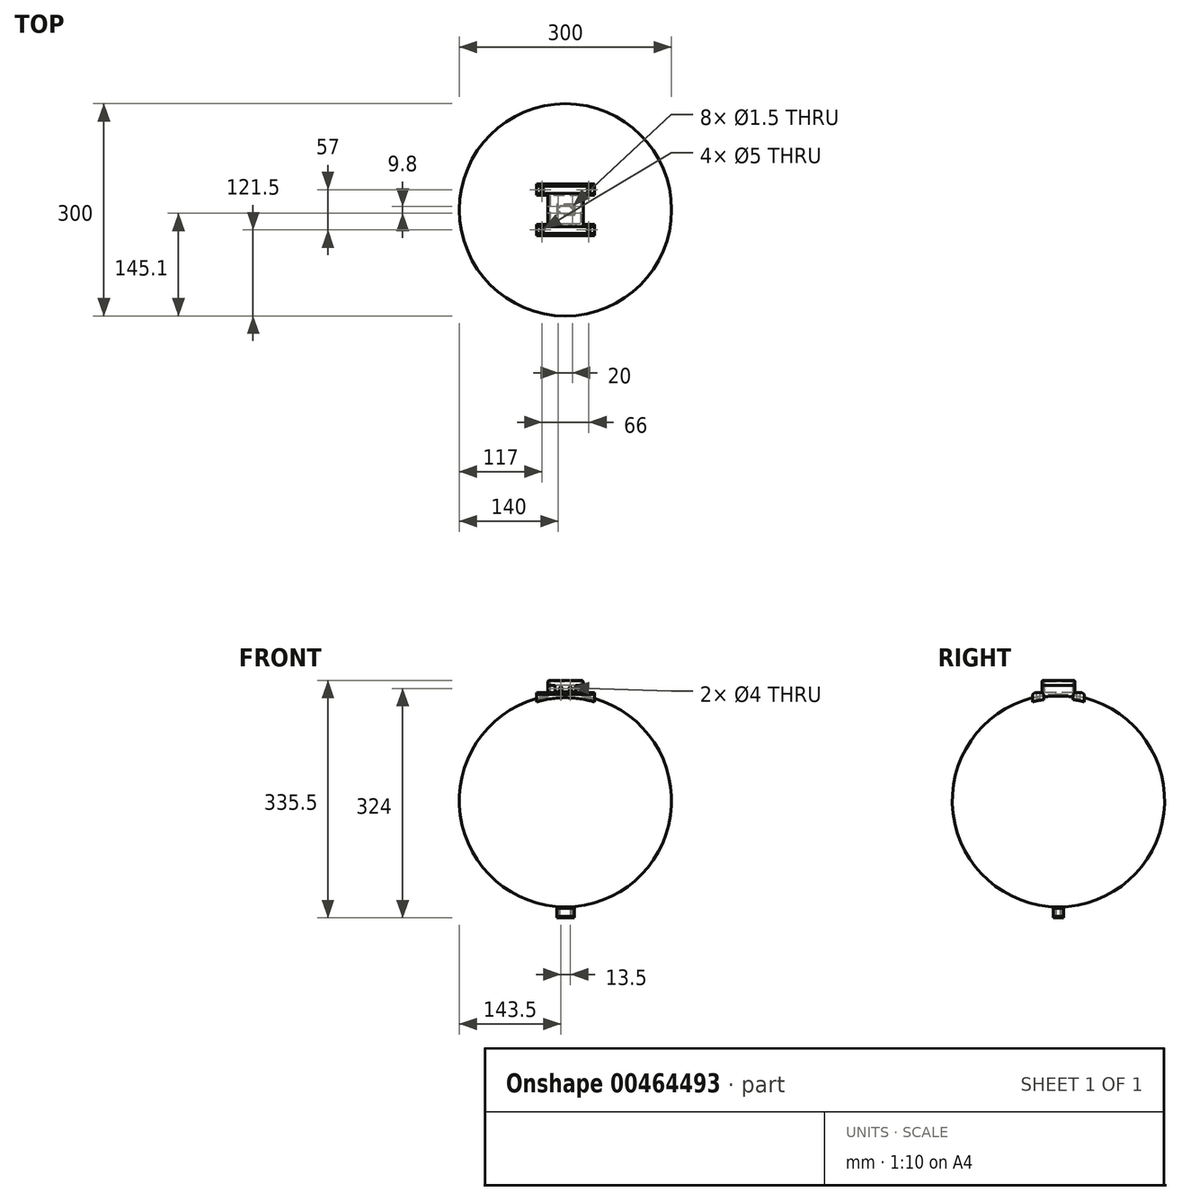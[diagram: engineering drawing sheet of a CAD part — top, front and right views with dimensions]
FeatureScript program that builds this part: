
annotation { "Feature Type Name" : "Feature", "Feature Type Description" : "" }
export const myFeature = defineFeature(function(context is Context, id is Id, definition is map)
    precondition{}
    {
        {
            assignVariable(context, id + "F0", {"name" : "R", "anyValue" : 150});
        }
        {
            assignVariable(context, id + "F1", {"name" : "T", "anyValue" : 3});
        }
        {
            assignVariable(context, id + "F2", {"name" : "t", "anyValue" : 2});
        }
        {
            var Q0;
            Q0=qCreatedBy(makeId("Right.planeOp"),FACE);
            var sketch = newSketch(context, id + "F3", { "sketchPlane" : qUnion([Q0])});
            skArc(sketch, "E0", {"start": v(0, -150) * mm, "mid": v(150, 0) * mm, "end": v(0, 150) * mm});
            skLineSegment(sketch, "E1", {"start": v(0, 133.29) * mm, "end": v(0, -166.2) * mm, "construction": true});
            skLineSegment(sketch, "E2", {"start": v(0, 150) * mm, "end": v(0, -150) * mm});
            skSolve(sketch);
        }
        {
            var Q0;
            Q0=makeQuery(id+"F3.imprint","IMPRINT",FACE,{"disambiguationData":[TD([[makeQuery(id+"F3.imprint","IMPRINT",EDGE,{"derivedFrom":sQuery(id+"F3.wireOp",EDGE,"E0")}),1.0]])]});
            var Q1;
            Q1=sQuery(id+"F3.wireOp",EDGE,"E1");
            revolve(context, id + "F4", {"entities" : qUnion([Q0]), "axis" : qUnion([Q1]), "revolveType" : RevolveType.FULL});
        }
        {
            var Q0;
            Q0=qCreatedBy(makeId("Top.planeOp"),FACE);
            cPlane(context, id + "F5", {"entities" : qUnion([Q0]), "cplaneType" : CPlaneType.OFFSET, "offset" : (getVariable(context, 'R') + getVariable(context, 'T')) * mm, "width" : 150 * mm, "height" : 150 * mm});
        }
        {
            var Q0;
            Q0=qCreatedBy(id+"F5.planeOp",FACE);
            var sketch = newSketch(context, id + "F6", { "sketchPlane" : qUnion([Q0])});
            skLineSegment(sketch, "E3.bottom", {"start": v(25, 36.5) * mm, "end": v(-25, 36.5) * mm});
            skLineSegment(sketch, "E3.top", {"start": v(25, -36.5) * mm, "end": v(-25, -36.5) * mm});
            skLineSegment(sketch, "E3.left", {"start": v(25, 20.5) * mm, "end": v(25, -20.5) * mm});
            skLineSegment(sketch, "E3.right", {"start": v(-25, 20.5) * mm, "end": v(-25, -20.5) * mm});
            skPoint(sketch, "E3.middle", {"position": v(0, 0) * mm});
            skLineSegment(sketch, "E4.bottom", {"start": v(-25, 36.5) * mm, "end": v(-41, 36.5) * mm});
            skLineSegment(sketch, "E4.top", {"start": v(-25, 20.5) * mm, "end": v(-41, 20.5) * mm});
            skLineSegment(sketch, "E4.right", {"start": v(-41, 36.5) * mm, "end": v(-41, 20.5) * mm});
            skLineSegment(sketch, "E5", {"start": v(0, 40.93) * mm, "end": v(0, -41.3) * mm, "construction": true});
            skLineSegment(sketch, "E6", {"start": v(40.69, 0) * mm, "end": v(-40.56, 0) * mm, "construction": true});
            skLineSegment(sketch, "E7.MirrorCS", {"start": v(25, 20.5) * mm, "end": v(41, 20.5) * mm});
            skLineSegment(sketch, "E8.MirrorCS", {"start": v(41, 36.5) * mm, "end": v(41, 20.5) * mm});
            skLineSegment(sketch, "E9.MirrorCS", {"start": v(25, 36.5) * mm, "end": v(41, 36.5) * mm});
            skLineSegment(sketch, "E10.MirrorCS", {"start": v(-25, -20.5) * mm, "end": v(-41, -20.5) * mm});
            skLineSegment(sketch, "E11.MirrorCS", {"start": v(-41, -36.5) * mm, "end": v(-41, -20.5) * mm});
            skLineSegment(sketch, "E12.MirrorCS", {"start": v(-25, -36.5) * mm, "end": v(-41, -36.5) * mm});
            skLineSegment(sketch, "E13.MirrorCS", {"start": v(25, -36.5) * mm, "end": v(41, -36.5) * mm});
            skLineSegment(sketch, "E14.MirrorCS", {"start": v(41, -36.5) * mm, "end": v(41, -20.5) * mm});
            skLineSegment(sketch, "E15.MirrorCS", {"start": v(25, -20.5) * mm, "end": v(41, -20.5) * mm});
            skLineSegment(sketch, "E16", {"start": v(-25, 20.5) * mm, "end": v(-41, 36.5) * mm, "construction": true});
            skLineSegment(sketch, "E17", {"start": v(-25, 36.5) * mm, "end": v(-41, 20.5) * mm, "construction": true});
            skCircle(sketch, "E18", {"center": v(-33, 28.5) * mm, "radius": 2.5 * mm});
            skCircle(sketch, "E19.MirrorC", {"center": v(33, 28.5) * mm, "radius": 2.5 * mm});
            skCircle(sketch, "E20.MirrorC", {"center": v(-33, -28.5) * mm, "radius": 2.5 * mm});
            skCircle(sketch, "E21.MirrorC", {"center": v(33, -28.5) * mm, "radius": 2.5 * mm});
            skSolve(sketch);
        }
        {
            var Q0;
            Q0=qSketchRegion(id+"F6",true);
            var Q1;
            Q1=makeQuery(id+"F4.opRevolve","SWEPT_FACE",FACE,{"disambiguationData":[OSD([sQuery(id+"F3.wireOp",EDGE,"E0")])]});
            extrude(context, id + "F7", {"entities" : qUnion([Q0]), "endBound" : BoundingType.UP_TO_SURFACE, "oppositeDirection" : true, "depth" : 25 * mm, "endBoundEntityFace" : qUnion([Q1]), "offsetDistance" : 25 * mm});
        }
        {
            var Q0;
            Q0=makeQuery(id+"F7.opExtrude","CAP_EDGE",EDGE,{"disambiguationData":[OSD([sQuery(id+"F6.wireOp",EDGE,"E3.bottom"),sQuery(id+"F6.wireOp",EDGE,"E4.bottom"),sQuery(id+"F6.wireOp",EDGE,"E9.MirrorCS")])],"isStart":true});
            var Q1;
            Q1=makeQuery(id+"F7.opExtrude","CAP_EDGE",EDGE,{"disambiguationData":[OSD([sQuery(id+"F6.wireOp",EDGE,"E3.top"),sQuery(id+"F6.wireOp",EDGE,"E12.MirrorCS"),sQuery(id+"F6.wireOp",EDGE,"E13.MirrorCS")])],"isStart":true});
            var Q2;
            Q2=makeQuery(id+"F7.opExtrude","CAP_EDGE",EDGE,{"disambiguationData":[OSD([sQuery(id+"F6.wireOp",EDGE,"E4.top")])],"isStart":true});
            var Q3;
            Q3=makeQuery(id+"F7.opExtrude","CAP_EDGE",EDGE,{"disambiguationData":[OSD([sQuery(id+"F6.wireOp",EDGE,"E7.MirrorCS")])],"isStart":true});
            var Q4;
            Q4=makeQuery(id+"F7.opExtrude","CAP_EDGE",EDGE,{"disambiguationData":[OSD([sQuery(id+"F6.wireOp",EDGE,"E15.MirrorCS")])],"isStart":true});
            var Q5;
            Q5=makeQuery(id+"F7.opExtrude","CAP_EDGE",EDGE,{"disambiguationData":[OSD([sQuery(id+"F6.wireOp",EDGE,"E10.MirrorCS")])],"isStart":true});
            chamfer(context, id + "F8", {"entities" : qUnion([Q0, Q1, Q2, Q3, Q4, Q5]), "width" : 3 * mm, "tangentPropagation" : true});
        }
        {
            var Q0;
            Q0=makeQuery(id+"F7.opExtrude","CAP_FACE",FACE,{"disambiguationData":[OSD([sQuery(id+"F6.wireOp",EDGE,"E3.bottom"),sQuery(id+"F6.wireOp",EDGE,"E3.top"),sQuery(id+"F6.wireOp",EDGE,"E3.left"),sQuery(id+"F6.wireOp",EDGE,"E3.right"),sQuery(id+"F6.wireOp",EDGE,"E4.bottom"),sQuery(id+"F6.wireOp",EDGE,"E4.top"),sQuery(id+"F6.wireOp",EDGE,"E4.right"),sQuery(id+"F6.wireOp",EDGE,"E7.MirrorCS"),sQuery(id+"F6.wireOp",EDGE,"E8.MirrorCS"),sQuery(id+"F6.wireOp",EDGE,"E9.MirrorCS"),sQuery(id+"F6.wireOp",EDGE,"E10.MirrorCS"),sQuery(id+"F6.wireOp",EDGE,"E11.MirrorCS"),sQuery(id+"F6.wireOp",EDGE,"E12.MirrorCS"),sQuery(id+"F6.wireOp",EDGE,"E13.MirrorCS"),sQuery(id+"F6.wireOp",EDGE,"E14.MirrorCS"),sQuery(id+"F6.wireOp",EDGE,"E15.MirrorCS"),sQuery(id+"F6.wireOp",EDGE,"E18"),sQuery(id+"F6.wireOp",EDGE,"E19.MirrorC"),sQuery(id+"F6.wireOp",EDGE,"E20.MirrorC"),sQuery(id+"F6.wireOp",EDGE,"E21.MirrorC")])],"isStart":true});
            var sketch = newSketch(context, id + "F9", { "sketchPlane" : qUnion([Q0])});
            skLineSegment(sketch, "E22.bottom", {"start": v(25, 23.5) * mm, "end": v(-25, 23.5) * mm});
            skLineSegment(sketch, "E22.top", {"start": v(25, -23.5) * mm, "end": v(15, -23.5) * mm});
            skLineSegment(sketch, "E22.left", {"start": v(25, 23.5) * mm, "end": v(25, -23.5) * mm});
            skLineSegment(sketch, "E22.right", {"start": v(-25, 23.5) * mm, "end": v(-25, -23.5) * mm});
            skPoint(sketch, "E22.middle", {"position": v(0, 0) * mm});
            skLineSegment(sketch, "E23.0", {"start": v(21.5, 20) * mm, "end": v(-21.5, 20) * mm});
            skLineSegment(sketch, "E23.1", {"start": v(21.5, 20) * mm, "end": v(21.5, -20) * mm});
            skLineSegment(sketch, "E23.2", {"start": v(21.5, -20) * mm, "end": v(15, -20) * mm});
            skLineSegment(sketch, "E23.3", {"start": v(-21.5, 20) * mm, "end": v(-21.5, -20) * mm});
            skLineSegment(sketch, "E24", {"start": v(-15, -20) * mm, "end": v(-15, -23.5) * mm});
            skLineSegment(sketch, "E25", {"start": v(15, -20) * mm, "end": v(15, -23.5) * mm});
            skLineSegment(sketch, "E26.trimOffspring", {"start": v(-15, -20) * mm, "end": v(-21.5, -20) * mm});
            skLineSegment(sketch, "E27.trimOffspring", {"start": v(-15, -23.5) * mm, "end": v(-25, -23.5) * mm});
            skSolve(sketch);
        }
        {
            var Q0;
            Q0=qSketchRegion(id+"F9",true);
            extrude(context, id + "F10", {"entities" : qUnion([Q0]), "operationType" : NewBodyOperationType.ADD, "depth" : 10 * mm, "offsetDistance" : 25 * mm});
        }
        {
            var Q0;
            Q0=makeQuery(id+"F10.opExtrude","CAP_FACE",FACE,{"disambiguationData":[OSD([sQuery(id+"F9.wireOp",EDGE,"E22.bottom"),sQuery(id+"F9.wireOp",EDGE,"E22.top"),sQuery(id+"F9.wireOp",EDGE,"E22.left"),sQuery(id+"F9.wireOp",EDGE,"E22.right"),sQuery(id+"F9.wireOp",EDGE,"E23.0"),sQuery(id+"F9.wireOp",EDGE,"E23.1"),sQuery(id+"F9.wireOp",EDGE,"E23.2"),sQuery(id+"F9.wireOp",EDGE,"E23.3"),sQuery(id+"F9.wireOp",EDGE,"E24"),sQuery(id+"F9.wireOp",EDGE,"E25"),sQuery(id+"F9.wireOp",EDGE,"E26.trimOffspring"),sQuery(id+"F9.wireOp",EDGE,"E27.trimOffspring")])],"isStart":false});
            var sketch = newSketch(context, id + "F11", { "sketchPlane" : qUnion([Q0])});
            skLineSegment(sketch, "E28.bottom", {"start": v(25, 23.5) * mm, "end": v(-25, 23.5) * mm});
            skLineSegment(sketch, "E28.top", {"start": v(25, -23.5) * mm, "end": v(-25, -23.5) * mm});
            skLineSegment(sketch, "E28.left", {"start": v(25, 23.5) * mm, "end": v(25, -23.5) * mm});
            skLineSegment(sketch, "E28.right", {"start": v(-25, 23.5) * mm, "end": v(-25, -23.5) * mm});
            skPoint(sketch, "E28.middle", {"position": v(0, 0) * mm});
            skLineSegment(sketch, "E29.0", {"start": v(21.5, 20) * mm, "end": v(-21.5, 20) * mm});
            skLineSegment(sketch, "E29.1", {"start": v(21.5, 20) * mm, "end": v(21.5, -20) * mm});
            skLineSegment(sketch, "E29.2", {"start": v(21.5, -20) * mm, "end": v(-21.5, -20) * mm});
            skLineSegment(sketch, "E29.3", {"start": v(-21.5, 20) * mm, "end": v(-21.5, -20) * mm});
            skSolve(sketch);
        }
        {
            var Q0;
            Q0=qSketchRegion(id+"F11",true);
            extrude(context, id + "F12", {"entities" : qUnion([Q0]), "depth" : 5 * mm, "offsetDistance" : 25 * mm});
        }
        {
            var Q0;
            Q0=makeQuery(id+"F12.opExtrude","CAP_FACE",FACE,{"disambiguationData":[OSD([sQuery(id+"F11.wireOp",EDGE,"E28.bottom"),sQuery(id+"F11.wireOp",EDGE,"E28.top"),sQuery(id+"F11.wireOp",EDGE,"E28.left"),sQuery(id+"F11.wireOp",EDGE,"E28.right"),sQuery(id+"F11.wireOp",EDGE,"E29.0"),sQuery(id+"F11.wireOp",EDGE,"E29.1"),sQuery(id+"F11.wireOp",EDGE,"E29.2"),sQuery(id+"F11.wireOp",EDGE,"E29.3")])],"isStart":false});
            var sketch = newSketch(context, id + "F13", { "sketchPlane" : qUnion([Q0])});
            skLineSegment(sketch, "E30.bottom", {"start": v(25, 23.5) * mm, "end": v(-25, 23.5) * mm});
            skLineSegment(sketch, "E30.top", {"start": v(25, -23.5) * mm, "end": v(-25, -23.5) * mm});
            skLineSegment(sketch, "E30.left", {"start": v(25, 23.5) * mm, "end": v(25, -23.5) * mm});
            skLineSegment(sketch, "E30.right", {"start": v(-25, 23.5) * mm, "end": v(-25, -23.5) * mm});
            skPoint(sketch, "E30.middle", {"position": v(0, 0) * mm});
            skSolve(sketch);
        }
        {
            var Q0;
            Q0=qSketchRegion(id+"F13",true);
            extrude(context, id + "F14", {"entities" : qUnion([Q0]), "operationType" : NewBodyOperationType.ADD, "depth" : 2 * mm, "offsetDistance" : 25 * mm});
        }
        {
            var Q0;
            Q0=makeQuery(id+"F14.opExtrude","CAP_FACE",FACE,{"disambiguationData":[OSD([sQuery(id+"F13.wireOp",EDGE,"E30.bottom"),sQuery(id+"F13.wireOp",EDGE,"E30.top"),sQuery(id+"F13.wireOp",EDGE,"E30.left"),sQuery(id+"F13.wireOp",EDGE,"E30.right")])],"isStart":false});
            var Q1;
            Q1=makeQuery(id+"F14.boolean.opBoolean","MERGE",EDGE,{"derivedFrom":[makeQuery(id+"F12.opExtrude","SWEPT_EDGE",EDGE,{"disambiguationData":[OSD([sQuery(id+"F11.wireOp",EDGE,"E28.top"),sQuery(id+"F11.wireOp",EDGE,"E28.right")])]}),makeQuery(id+"F14.opExtrude","SWEPT_EDGE",EDGE,{"disambiguationData":[OSD([sQuery(id+"F13.wireOp",EDGE,"E30.top"),sQuery(id+"F13.wireOp",EDGE,"E30.right")])]})]});
            var Q2;
            Q2=makeQuery(id+"F10.opExtrude","SWEPT_EDGE",EDGE,{"disambiguationData":[OSD([sQuery(id+"F6.wireOp",EDGE,"E3.bottom"),sQuery(id+"F6.wireOp",EDGE,"E3.top"),sQuery(id+"F6.wireOp",EDGE,"E3.left"),sQuery(id+"F6.wireOp",EDGE,"E3.right"),sQuery(id+"F6.wireOp",EDGE,"E4.bottom"),sQuery(id+"F6.wireOp",EDGE,"E4.top"),sQuery(id+"F6.wireOp",EDGE,"E4.right"),sQuery(id+"F6.wireOp",EDGE,"E7.MirrorCS"),sQuery(id+"F6.wireOp",EDGE,"E8.MirrorCS"),sQuery(id+"F6.wireOp",EDGE,"E9.MirrorCS"),sQuery(id+"F6.wireOp",EDGE,"E10.MirrorCS"),sQuery(id+"F6.wireOp",EDGE,"E11.MirrorCS"),sQuery(id+"F6.wireOp",EDGE,"E12.MirrorCS"),sQuery(id+"F6.wireOp",EDGE,"E13.MirrorCS"),sQuery(id+"F6.wireOp",EDGE,"E14.MirrorCS"),sQuery(id+"F6.wireOp",EDGE,"E15.MirrorCS"),sQuery(id+"F6.wireOp",EDGE,"E18"),sQuery(id+"F6.wireOp",EDGE,"E19.MirrorC"),sQuery(id+"F6.wireOp",EDGE,"E20.MirrorC"),sQuery(id+"F6.wireOp",EDGE,"E21.MirrorC"),sQuery(id+"F9.wireOp",EDGE,"E22.right"),sQuery(id+"F9.wireOp",EDGE,"E27.trimOffspring")])]});
            var Q3;
            Q3=makeQuery(id+"F10.opExtrude","SWEPT_EDGE",EDGE,{"disambiguationData":[OSD([sQuery(id+"F6.wireOp",EDGE,"E3.bottom"),sQuery(id+"F6.wireOp",EDGE,"E3.top"),sQuery(id+"F6.wireOp",EDGE,"E3.left"),sQuery(id+"F6.wireOp",EDGE,"E3.right"),sQuery(id+"F6.wireOp",EDGE,"E4.bottom"),sQuery(id+"F6.wireOp",EDGE,"E4.top"),sQuery(id+"F6.wireOp",EDGE,"E4.right"),sQuery(id+"F6.wireOp",EDGE,"E7.MirrorCS"),sQuery(id+"F6.wireOp",EDGE,"E8.MirrorCS"),sQuery(id+"F6.wireOp",EDGE,"E9.MirrorCS"),sQuery(id+"F6.wireOp",EDGE,"E10.MirrorCS"),sQuery(id+"F6.wireOp",EDGE,"E11.MirrorCS"),sQuery(id+"F6.wireOp",EDGE,"E12.MirrorCS"),sQuery(id+"F6.wireOp",EDGE,"E13.MirrorCS"),sQuery(id+"F6.wireOp",EDGE,"E14.MirrorCS"),sQuery(id+"F6.wireOp",EDGE,"E15.MirrorCS"),sQuery(id+"F6.wireOp",EDGE,"E18"),sQuery(id+"F6.wireOp",EDGE,"E19.MirrorC"),sQuery(id+"F6.wireOp",EDGE,"E20.MirrorC"),sQuery(id+"F6.wireOp",EDGE,"E21.MirrorC"),sQuery(id+"F9.wireOp",EDGE,"E22.bottom"),sQuery(id+"F9.wireOp",EDGE,"E22.right")])]});
            var Q4;
            Q4=makeQuery(id+"F14.boolean.opBoolean","MERGE",EDGE,{"derivedFrom":[makeQuery(id+"F12.opExtrude","SWEPT_EDGE",EDGE,{"disambiguationData":[OSD([sQuery(id+"F11.wireOp",EDGE,"E28.bottom"),sQuery(id+"F11.wireOp",EDGE,"E28.right")])]}),makeQuery(id+"F14.opExtrude","SWEPT_EDGE",EDGE,{"disambiguationData":[OSD([sQuery(id+"F13.wireOp",EDGE,"E30.bottom"),sQuery(id+"F13.wireOp",EDGE,"E30.right")])]})]});
            var Q5;
            Q5=makeQuery(id+"F10.opExtrude","SWEPT_EDGE",EDGE,{"disambiguationData":[OSD([sQuery(id+"F6.wireOp",EDGE,"E3.bottom"),sQuery(id+"F6.wireOp",EDGE,"E3.top"),sQuery(id+"F6.wireOp",EDGE,"E3.left"),sQuery(id+"F6.wireOp",EDGE,"E3.right"),sQuery(id+"F6.wireOp",EDGE,"E4.bottom"),sQuery(id+"F6.wireOp",EDGE,"E4.top"),sQuery(id+"F6.wireOp",EDGE,"E4.right"),sQuery(id+"F6.wireOp",EDGE,"E7.MirrorCS"),sQuery(id+"F6.wireOp",EDGE,"E8.MirrorCS"),sQuery(id+"F6.wireOp",EDGE,"E9.MirrorCS"),sQuery(id+"F6.wireOp",EDGE,"E10.MirrorCS"),sQuery(id+"F6.wireOp",EDGE,"E11.MirrorCS"),sQuery(id+"F6.wireOp",EDGE,"E12.MirrorCS"),sQuery(id+"F6.wireOp",EDGE,"E13.MirrorCS"),sQuery(id+"F6.wireOp",EDGE,"E14.MirrorCS"),sQuery(id+"F6.wireOp",EDGE,"E15.MirrorCS"),sQuery(id+"F6.wireOp",EDGE,"E18"),sQuery(id+"F6.wireOp",EDGE,"E19.MirrorC"),sQuery(id+"F6.wireOp",EDGE,"E20.MirrorC"),sQuery(id+"F6.wireOp",EDGE,"E21.MirrorC"),sQuery(id+"F9.wireOp",EDGE,"E22.top"),sQuery(id+"F9.wireOp",EDGE,"E22.left")])]});
            var Q6;
            Q6=makeQuery(id+"F14.boolean.opBoolean","MERGE",EDGE,{"derivedFrom":[makeQuery(id+"F12.opExtrude","SWEPT_EDGE",EDGE,{"disambiguationData":[OSD([sQuery(id+"F11.wireOp",EDGE,"E28.top"),sQuery(id+"F11.wireOp",EDGE,"E28.left")])]}),makeQuery(id+"F14.opExtrude","SWEPT_EDGE",EDGE,{"disambiguationData":[OSD([sQuery(id+"F13.wireOp",EDGE,"E30.top"),sQuery(id+"F13.wireOp",EDGE,"E30.left")])]})]});
            var Q7;
            Q7=makeQuery(id+"F10.opExtrude","SWEPT_EDGE",EDGE,{"disambiguationData":[OSD([sQuery(id+"F6.wireOp",EDGE,"E3.bottom"),sQuery(id+"F6.wireOp",EDGE,"E3.top"),sQuery(id+"F6.wireOp",EDGE,"E3.left"),sQuery(id+"F6.wireOp",EDGE,"E3.right"),sQuery(id+"F6.wireOp",EDGE,"E4.bottom"),sQuery(id+"F6.wireOp",EDGE,"E4.top"),sQuery(id+"F6.wireOp",EDGE,"E4.right"),sQuery(id+"F6.wireOp",EDGE,"E7.MirrorCS"),sQuery(id+"F6.wireOp",EDGE,"E8.MirrorCS"),sQuery(id+"F6.wireOp",EDGE,"E9.MirrorCS"),sQuery(id+"F6.wireOp",EDGE,"E10.MirrorCS"),sQuery(id+"F6.wireOp",EDGE,"E11.MirrorCS"),sQuery(id+"F6.wireOp",EDGE,"E12.MirrorCS"),sQuery(id+"F6.wireOp",EDGE,"E13.MirrorCS"),sQuery(id+"F6.wireOp",EDGE,"E14.MirrorCS"),sQuery(id+"F6.wireOp",EDGE,"E15.MirrorCS"),sQuery(id+"F6.wireOp",EDGE,"E18"),sQuery(id+"F6.wireOp",EDGE,"E19.MirrorC"),sQuery(id+"F6.wireOp",EDGE,"E20.MirrorC"),sQuery(id+"F6.wireOp",EDGE,"E21.MirrorC"),sQuery(id+"F9.wireOp",EDGE,"E22.bottom"),sQuery(id+"F9.wireOp",EDGE,"E22.left")])]});
            var Q8;
            Q8=makeQuery(id+"F14.boolean.opBoolean","MERGE",EDGE,{"derivedFrom":[makeQuery(id+"F12.opExtrude","SWEPT_EDGE",EDGE,{"disambiguationData":[OSD([sQuery(id+"F11.wireOp",EDGE,"E28.bottom"),sQuery(id+"F11.wireOp",EDGE,"E28.left")])]}),makeQuery(id+"F14.opExtrude","SWEPT_EDGE",EDGE,{"disambiguationData":[OSD([sQuery(id+"F13.wireOp",EDGE,"E30.bottom"),sQuery(id+"F13.wireOp",EDGE,"E30.left")])]})]});
            fillet(context, id + "F15", {"entities" : qUnion([Q0, Q1, Q2, Q3, Q4, Q5, Q6, Q7, Q8]), "radius" : 2.5 * mm, "tangentPropagation" : true, "allowEdgeOverflow" : false});
        }
        {
            var Q0;
            Q0=makeQuery(id+"F12.opExtrude","CAP_FACE",FACE,{"disambiguationData":[OSD([sQuery(id+"F11.wireOp",EDGE,"E28.bottom"),sQuery(id+"F11.wireOp",EDGE,"E28.top"),sQuery(id+"F11.wireOp",EDGE,"E28.left"),sQuery(id+"F11.wireOp",EDGE,"E28.right"),sQuery(id+"F11.wireOp",EDGE,"E29.0"),sQuery(id+"F11.wireOp",EDGE,"E29.1"),sQuery(id+"F11.wireOp",EDGE,"E29.2"),sQuery(id+"F11.wireOp",EDGE,"E29.3")])],"isStart":true});
            var sketch = newSketch(context, id + "F16", { "sketchPlane" : qUnion([Q0])});
            skLineSegment(sketch, "E31.bottom", {"start": v(-14.5, 23.5) * mm, "end": v(14.5, 23.5) * mm});
            skLineSegment(sketch, "E31.top", {"start": v(-14.5, 20) * mm, "end": v(14.5, 20) * mm});
            skLineSegment(sketch, "E31.left", {"start": v(-14.5, 23.5) * mm, "end": v(-14.5, 20) * mm});
            skLineSegment(sketch, "E31.right", {"start": v(14.5, 23.5) * mm, "end": v(14.5, 20) * mm});
            skSolve(sketch);
        }
        {
            var Q0;
            Q0=qSketchRegion(id+"F16",true);
            extrude(context, id + "F17", {"entities" : qUnion([Q0]), "operationType" : NewBodyOperationType.ADD, "depth" : 9 * mm, "offsetDistance" : 25 * mm});
        }
        {
            var Q0;
            Q0=makeQuery(id+"F17.boolean.opBoolean","MERGE",FACE,{"derivedFrom":[makeQuery(id+"F14.boolean.opBoolean","MERGE",FACE,{"derivedFrom":[makeQuery(id+"F12.opExtrude","SWEPT_FACE",FACE,{"disambiguationData":[OSD([sQuery(id+"F11.wireOp",EDGE,"E28.top")])]}),makeQuery(id+"F14.opExtrude","SWEPT_FACE",FACE,{"disambiguationData":[OSD([sQuery(id+"F13.wireOp",EDGE,"E30.top")])]})]}),makeQuery(id+"F17.opExtrude","SWEPT_FACE",FACE,{"disambiguationData":[OSD([sQuery(id+"F16.wireOp",EDGE,"E31.bottom")])]})]});
            var sketch = newSketch(context, id + "F18", { "sketchPlane" : qUnion([Q0])});
            skCircle(sketch, "E32", {"center": v(-6.5, 158.5) * mm, "radius": 2 * mm});
            skCircle(sketch, "E33", {"center": v(7, 158.5) * mm, "radius": 2 * mm});
            skSolve(sketch);
        }
        {
            var Q0;
            Q0=qSketchRegion(id+"F18",true);
            var Q1;
            Q1=makeQuery(id+"F17.boolean.opBoolean","MERGE",FACE,{"derivedFrom":[makeQuery(id+"F12.opExtrude","SWEPT_FACE",FACE,{"disambiguationData":[OSD([sQuery(id+"F11.wireOp",EDGE,"E29.2")])]}),makeQuery(id+"F17.opExtrude","SWEPT_FACE",FACE,{"disambiguationData":[OSD([sQuery(id+"F16.wireOp",EDGE,"E31.top")])]})]});
            extrude(context, id + "F19", {"entities" : qUnion([Q0]), "operationType" : NewBodyOperationType.REMOVE, "endBound" : BoundingType.UP_TO_SURFACE, "oppositeDirection" : true, "depth" : 25 * mm, "endBoundEntityFace" : qUnion([Q1]), "offsetDistance" : 25 * mm});
        }
        {
            var Q0;
            Q0=qCreatedBy(makeId("Top.planeOp"),FACE);
            cPlane(context, id + "F20", {"entities" : qUnion([Q0]), "cplaneType" : CPlaneType.OFFSET, "offset" : (getVariable(context, 'R') + getVariable(context, 't')) * mm, "oppositeDirection" : true, "width" : 150 * mm, "height" : 150 * mm});
        }
        {
            var Q0;
            Q0=qCreatedBy(id+"F20.planeOp",FACE);
            var sketch = newSketch(context, id + "F21", { "sketchPlane" : qUnion([Q0])});
            skLineSegment(sketch, "E34.bottom", {"start": v(12.5, 7.15) * mm, "end": v(-12.5, 7.15) * mm});
            skLineSegment(sketch, "E34.top", {"start": v(12.5, -7.15) * mm, "end": v(-12.5, -7.15) * mm});
            skLineSegment(sketch, "E34.left", {"start": v(12.5, 7.15) * mm, "end": v(12.5, -7.15) * mm});
            skLineSegment(sketch, "E34.right", {"start": v(-12.5, 7.15) * mm, "end": v(-12.5, -7.15) * mm});
            skPoint(sketch, "E34.middle", {"position": v(0, 0) * mm});
            skLineSegment(sketch, "E35.0", {"start": v(13.5, -8.15) * mm, "end": v(-12.5, -8.15) * mm});
            skLineSegment(sketch, "E35.1", {"start": v(13.5, 8.15) * mm, "end": v(13.5, -8.15) * mm});
            skLineSegment(sketch, "E35.2", {"start": v(13.5, 8.15) * mm, "end": v(-12.5, 8.15) * mm});
            skLineSegment(sketch, "E36", {"start": v(-12.5, -8.15) * mm, "end": v(-12.5, -7.15) * mm});
            skLineSegment(sketch, "E37", {"start": v(-12.5, 8.15) * mm, "end": v(-12.5, 7.15) * mm});
            skSolve(sketch);
        }
        {
            var Q0;
            Q0=qSketchRegion(id+"F21",true);
            extrude(context, id + "F22", {"entities" : qUnion([Q0]), "depth" : 1 * mm, "offsetDistance" : 25 * mm});
        }
        {
            var Q0;
            Q0=makeQuery(id+"F21.imprint","IMPRINT",FACE,{"disambiguationData":[TD([[makeQuery(id+"F21.imprint","IMPRINT",EDGE,{"derivedFrom":sQuery(id+"F21.wireOp",EDGE,"E34.bottom")}),1.0]])]});
            extrude(context, id + "F23", {"entities" : qUnion([Q0]), "operationType" : NewBodyOperationType.ADD, "oppositeDirection" : true, "depth" : 1.5 * mm, "offsetDistance" : 25 * mm});
        }
        {
            var Q0;
            Q0=makeQuery(id+"F23.opExtrude","CAP_FACE",FACE,{"disambiguationData":[OSD([sQuery(id+"F21.wireOp",EDGE,"E34.bottom"),sQuery(id+"F21.wireOp",EDGE,"E34.top"),sQuery(id+"F21.wireOp",EDGE,"E34.left"),sQuery(id+"F21.wireOp",EDGE,"E34.right")])],"isStart":false});
            var sketch = newSketch(context, id + "F24", { "sketchPlane" : qUnion([Q0])});
            skLineSegment(sketch, "E38.bottom", {"start": v(12.5, 7.15) * mm, "end": v(-12.5, 7.15) * mm});
            skLineSegment(sketch, "E38.top", {"start": v(12.5, -7.15) * mm, "end": v(-12.5, -7.15) * mm});
            skLineSegment(sketch, "E38.left", {"start": v(12.5, 7.15) * mm, "end": v(12.5, -7.15) * mm});
            skLineSegment(sketch, "E38.right", {"start": v(-12.5, 7.15) * mm, "end": v(-12.5, 3) * mm});
            skPoint(sketch, "E38.middle", {"position": v(0, 0) * mm});
            skLineSegment(sketch, "E39.0", {"start": v(7.5, 5.65) * mm, "end": v(-7.5, 5.65) * mm});
            skLineSegment(sketch, "E39.1", {"start": v(11, 3) * mm, "end": v(11, -3) * mm});
            skLineSegment(sketch, "E39.2", {"start": v(7.5, -5.65) * mm, "end": v(-7.5, -5.65) * mm});
            skLineSegment(sketch, "E40", {"start": v(-7.5, 3) * mm, "end": v(-12.5, 3) * mm});
            skLineSegment(sketch, "E41.trimOffspring", {"start": v(-12.5, -3) * mm, "end": v(-12.5, -7.15) * mm});
            skLineSegment(sketch, "E42", {"start": v(-7.5, 3) * mm, "end": v(-7.5, 5.65) * mm});
            skLineSegment(sketch, "E43", {"start": v(-12.5, 0) * mm, "end": v(12.5, 0) * mm, "construction": true});
            skLineSegment(sketch, "E44", {"start": v(0, 7.15) * mm, "end": v(0, -7.15) * mm, "construction": true});
            skLineSegment(sketch, "E45.MirrorCS", {"start": v(7.5, 3) * mm, "end": v(7.5, 5.65) * mm});
            skLineSegment(sketch, "E46.MirrorCS", {"start": v(7.5, 3) * mm, "end": v(12.5, 3) * mm});
            skLineSegment(sketch, "E47.MirrorCS", {"start": v(7.5, -3) * mm, "end": v(7.5, -5.65) * mm});
            skLineSegment(sketch, "E48.MirrorCS", {"start": v(7.5, -3) * mm, "end": v(12.5, -3) * mm});
            skLineSegment(sketch, "E49.MirrorCS", {"start": v(-7.5, -3) * mm, "end": v(-7.5, -5.65) * mm});
            skLineSegment(sketch, "E50.MirrorCS", {"start": v(-7.5, -3) * mm, "end": v(-12.5, -3) * mm});
            skSolve(sketch);
        }
        {
            var Q0;
            Q0=qSketchRegion(id+"F24",true);
            extrude(context, id + "F25", {"entities" : qUnion([Q0]), "operationType" : NewBodyOperationType.ADD, "depth" : 10 * mm, "offsetDistance" : 25 * mm});
        }
        {
            var Q0;
            Q0=makeQuery(id+"F25.opExtrude","CAP_FACE",FACE,{"disambiguationData":[OSD([sQuery(id+"F24.wireOp",EDGE,"E38.bottom"),sQuery(id+"F24.wireOp",EDGE,"E38.top"),sQuery(id+"F24.wireOp",EDGE,"E38.left"),sQuery(id+"F24.wireOp",EDGE,"E38.right"),sQuery(id+"F24.wireOp",EDGE,"E39.0"),sQuery(id+"F24.wireOp",EDGE,"E39.1"),sQuery(id+"F24.wireOp",EDGE,"E39.2"),sQuery(id+"F24.wireOp",EDGE,"E39.3"),sQuery(id+"F24.wireOp",EDGE,"q1GNPKCj-zdpP-4HE7-qGwj-qCHKBDN4xecH.bottom"),sQuery(id+"F24.wireOp",EDGE,"q1GNPKCj-zdpP-4HE7-qGwj-qCHKBDN4xecH.top"),sQuery(id+"F24.wireOp",EDGE,"q1GNPKCj-zdpP-4HE7-qGwj-qCHKBDN4xecH.left"),sQuery(id+"F24.wireOp",EDGE,"q1GNPKCj-zdpP-4HE7-qGwj-qCHKBDN4xecH.right"),sQuery(id+"F24.wireOp",EDGE,"9ayAVEPv-Baah-zfO2-cBUv-Tw3wUvXcA2ry.bottom"),sQuery(id+"F24.wireOp",EDGE,"9ayAVEPv-Baah-zfO2-cBUv-Tw3wUvXcA2ry.top"),sQuery(id+"F24.wireOp",EDGE,"9ayAVEPv-Baah-zfO2-cBUv-Tw3wUvXcA2ry.right"),sQuery(id+"F24.wireOp",EDGE,"KkwPjkcE-YuFN-ka4I-ebTg-GOtfCpxhzfaz.bottom"),sQuery(id+"F24.wireOp",EDGE,"KkwPjkcE-YuFN-ka4I-ebTg-GOtfCpxhzfaz.top"),sQuery(id+"F24.wireOp",EDGE,"KkwPjkcE-YuFN-ka4I-ebTg-GOtfCpxhzfaz.left"),sQuery(id+"F24.wireOp",EDGE,"KkwPjkcE-YuFN-ka4I-ebTg-GOtfCpxhzfaz.right"),sQuery(id+"F24.wireOp",EDGE,"bSv0btmW-40Pc-zO7x-vEyI-oRbhWPC2zANg.bottom"),sQuery(id+"F24.wireOp",EDGE,"bSv0btmW-40Pc-zO7x-vEyI-oRbhWPC2zANg.top"),sQuery(id+"F24.wireOp",EDGE,"bSv0btmW-40Pc-zO7x-vEyI-oRbhWPC2zANg.left"),sQuery(id+"F24.wireOp",EDGE,"bSv0btmW-40Pc-zO7x-vEyI-oRbhWPC2zANg.right"),sQuery(id+"F24.wireOp",EDGE,"E40"),sQuery(id+"F24.wireOp",EDGE,"pJDALD0U-aj2j-U3tK-gEwn-GPk6D3x3Uf9U"),sQuery(id+"F24.wireOp",EDGE,"8bf2260b-e43b-4eec-a6cd-762596e679c8.trimOffspring"),sQuery(id+"F24.wireOp",EDGE,"E41.trimOffspring")])],"isStart":false});
            var sketch = newSketch(context, id + "F26", { "sketchPlane" : qUnion([Q0])});
            skLineSegment(sketch, "E51.bottom", {"start": v(-12.5, 7.15) * mm, "end": v(12.5, 7.15) * mm});
            skLineSegment(sketch, "E51.top", {"start": v(-12.5, -7.15) * mm, "end": v(12.5, -7.15) * mm});
            skLineSegment(sketch, "E51.left", {"start": v(-12.5, 7.15) * mm, "end": v(-12.5, -7.15) * mm});
            skLineSegment(sketch, "E51.right", {"start": v(12.5, 7.15) * mm, "end": v(12.5, -7.15) * mm});
            skSolve(sketch);
        }
        {
            var Q0;
            Q0=qSketchRegion(id+"F26",true);
            extrude(context, id + "F27", {"entities" : qUnion([Q0]), "depth" : 2 * mm, "offsetDistance" : 25 * mm});
        }
        {
            var Q0;
            Q0=makeQuery(id+"F27.opExtrude","CAP_FACE",FACE,{"disambiguationData":[OSD([sQuery(id+"F26.wireOp",EDGE,"E51.bottom"),sQuery(id+"F26.wireOp",EDGE,"E51.top"),sQuery(id+"F26.wireOp",EDGE,"E51.left"),sQuery(id+"F26.wireOp",EDGE,"E51.right")])],"isStart":false});
            var sketch = newSketch(context, id + "F28", { "sketchPlane" : qUnion([Q0])});
            skCircle(sketch, "E52", {"center": v(-10, 4.9) * mm, "radius": 0.75 * mm});
            skLineSegment(sketch, "E53", {"start": v(0, 7.15) * mm, "end": v(0, -7.15) * mm, "construction": true});
            skLineSegment(sketch, "E54", {"start": v(12.5, 0) * mm, "end": v(-12.5, 0) * mm, "construction": true});
            skCircle(sketch, "E55.MirrorC", {"center": v(-10, -4.9) * mm, "radius": 0.75 * mm});
            skCircle(sketch, "E56.MirrorC", {"center": v(10, 4.9) * mm, "radius": 0.75 * mm});
            skCircle(sketch, "E57.MirrorC", {"center": v(10, -4.9) * mm, "radius": 0.75 * mm});
            skSolve(sketch);
        }
        {
            var Q0;
            Q0=qSketchRegion(id+"F28",true);
            var Q1;
            Q1=makeQuery(id+"F22.opExtrude","CAP_FACE",FACE,{"disambiguationData":[OSD([sQuery(id+"F21.wireOp",EDGE,"E34.right"),sQuery(id+"F21.wireOp",EDGE,"E35.0"),sQuery(id+"F21.wireOp",EDGE,"E35.1"),sQuery(id+"F21.wireOp",EDGE,"E35.2"),sQuery(id+"F21.wireOp",EDGE,"E36"),sQuery(id+"F21.wireOp",EDGE,"E37")])],"isStart":false});
            extrude(context, id + "F29", {"entities" : qUnion([Q0]), "operationType" : NewBodyOperationType.REMOVE, "endBound" : BoundingType.UP_TO_SURFACE, "oppositeDirection" : true, "depth" : 25 * mm, "endBoundEntityFace" : qUnion([Q1]), "offsetDistance" : 25 * mm});
        }
    });
